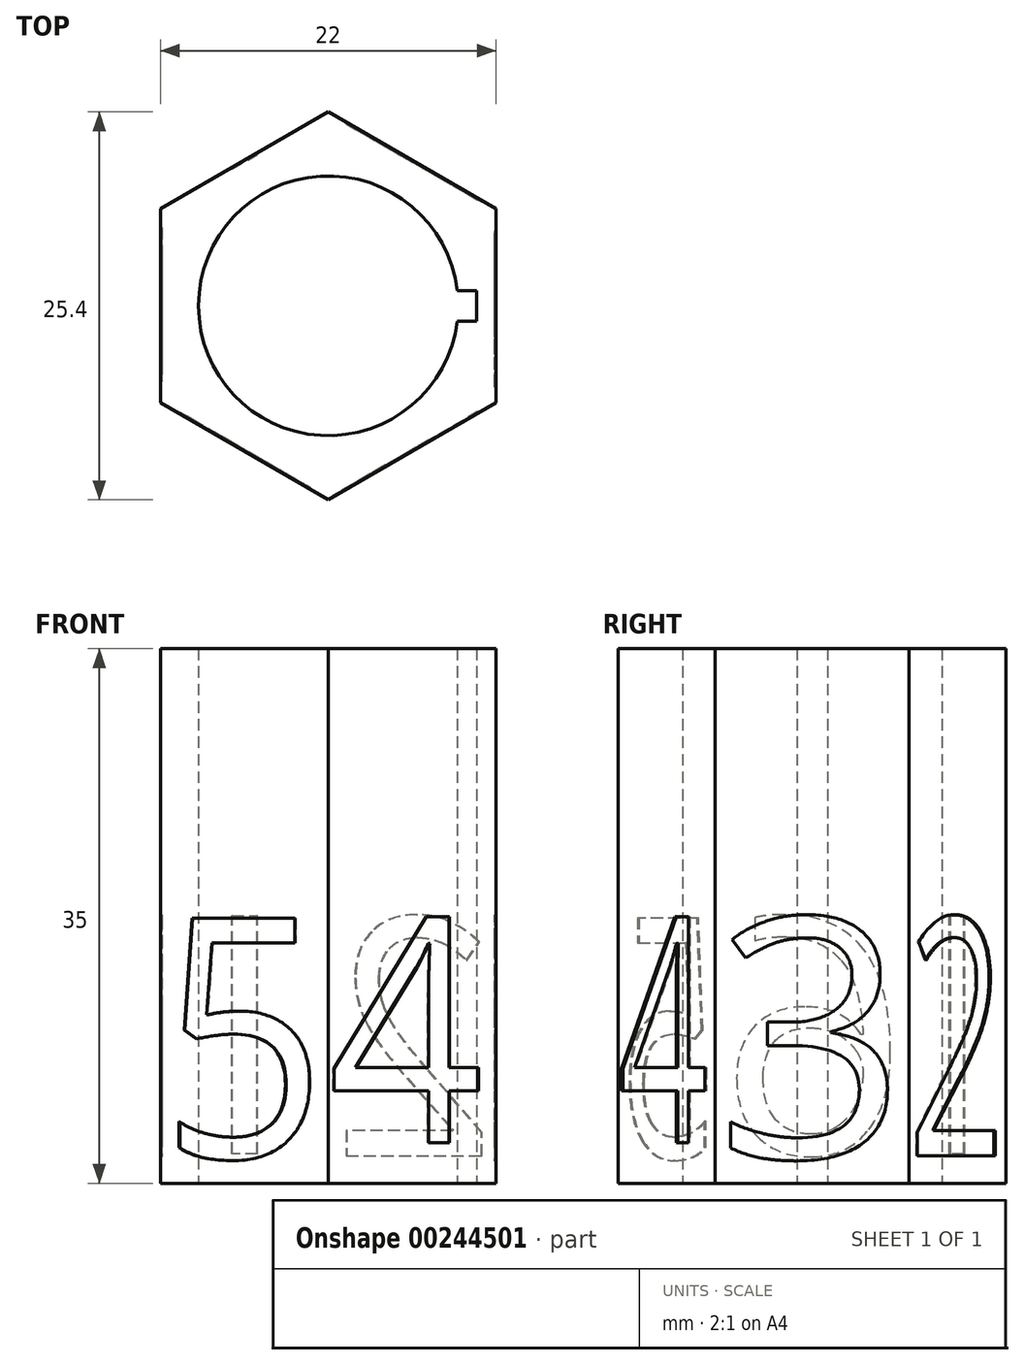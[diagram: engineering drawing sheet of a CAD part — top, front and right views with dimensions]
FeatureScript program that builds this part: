
annotation { "Feature Type Name" : "Feature", "Feature Type Description" : "" }
export const myFeature = defineFeature(function(context is Context, id is Id, definition is map)
    precondition{}
    {
        {
            var Q0;
            Q0=qCreatedBy(makeId("Top.planeOp"),FACE);
            var sketch = newSketch(context, id + "F0", { "sketchPlane" : qUnion([Q0])});
            skCircle(sketch, "E0", {"center": v(0, 0) * mm, "radius": 12.7 * mm});
            skCircle(sketch, "E1.cCircle", {"center": v(0, 0) * mm, "radius": 12.7 * mm, "construction": true});
            skLineSegment(sketch, "E1.0", {"start": v(0, 12.7) * mm, "end": v(11, 6.35) * mm});
            skLineSegment(sketch, "E1.1", {"start": v(11, 6.35) * mm, "end": v(11, -6.35) * mm});
            skLineSegment(sketch, "E1.2", {"start": v(11, -6.35) * mm, "end": v(0, -12.7) * mm});
            skLineSegment(sketch, "E1.3", {"start": v(0, -12.7) * mm, "end": v(-11, -6.35) * mm});
            skLineSegment(sketch, "E1.4", {"start": v(-11, -6.35) * mm, "end": v(-11, 6.35) * mm});
            skLineSegment(sketch, "E1.5", {"start": v(-11, 6.35) * mm, "end": v(0, 12.7) * mm});
            skSolve(sketch);
        }
        {
            var Q0;
            Q0=makeQuery(id+"F0.imprint","IMPRINT",FACE,{"disambiguationData":[TD([[makeQuery(id+"F0.imprint","IMPRINT",EDGE,{"derivedFrom":sQuery(id+"F0.wireOp",EDGE,"E1.0")}),-1.0]])]});
            extrude(context, id + "F1", {"entities" : qUnion([Q0]), "depth" : 35 * mm});
        }
        {
            var Q0;
            Q0=makeQuery(id+"F1.opExtrude","CAP_FACE",FACE,{"disambiguationData":[OSD([sQuery(id+"F0.wireOp",EDGE,"E1.0"),sQuery(id+"F0.wireOp",EDGE,"E1.1"),sQuery(id+"F0.wireOp",EDGE,"E1.2"),sQuery(id+"F0.wireOp",EDGE,"E1.3"),sQuery(id+"F0.wireOp",EDGE,"E1.4"),sQuery(id+"F0.wireOp",EDGE,"E1.5")])],"isStart":true});
            var sketch = newSketch(context, id + "F2", { "sketchPlane" : qUnion([Q0])});
            skArc(sketch, "E2", {"start": v(8.44, 1) * mm, "mid": v(-8.5, 0) * mm, "end": v(8.44, -1) * mm});
            skLineSegment(sketch, "E3", {"start": v(9.72, 1) * mm, "end": v(8.44, 1) * mm});
            skLineSegment(sketch, "E4", {"start": v(8.44, 1) * mm, "end": v(9.72, 1) * mm});
            skLineSegment(sketch, "E5", {"start": v(9.72, -1) * mm, "end": v(8.44, -1) * mm});
            skLineSegment(sketch, "E6", {"start": v(8.44, -1) * mm, "end": v(9.72, -1) * mm});
            skLineSegment(sketch, "E7", {"start": v(9.72, -1) * mm, "end": v(9.72, 1) * mm});
            skPoint(sketch, "E8.end.orphan", {"position": v(11, -1) * mm});
            skPoint(sketch, "E9.end.orphan", {"position": v(11, 1) * mm});
            skPoint(sketch, "E9.start.orphan", {"position": v(11, 0) * mm});
            skSolve(sketch);
        }
        {
            var Q0;
            Q0 = qSketchRegion(id + "F2", true);
            extrude(context, id + "F3", {"entities" : qUnion([Q0]), "operationType" : NewBodyOperationType.REMOVE, "oppositeDirection" : true, "depth" : 45 * mm});
        }
        {
            var Q0;
            Q0=makeQuery(id+"F1.opExtrude","SWEPT_FACE",FACE,{"disambiguationData":[OSD([sQuery(id+"F0.wireOp",EDGE,"E1.1")])]});
            var sketch = newSketch(context, id + "F4", { "sketchPlane" : qUnion([Q0])});
            skText(sketch, "E10", { "text": "3", "fontName": "OpenSans-Regular.ttf"});
            const initialGuessF4  = {"E10": [-0.00635, 0.00168, 1, 0, 0.01582]};
            skSetInitialGuess(sketch, initialGuessF4);
            skSolve(sketch);
        }
        {
            var Q0;
            Q0 = qSketchRegion(id + "F4", true);
            extrude(context, id + "F5", {"entities" : qUnion([Q0]), "operationType" : NewBodyOperationType.REMOVE, "oppositeDirection" : true, "depth" : .1 * mm});
        }
        {
            var Q0;
            Q0=makeQuery(id+"F1.opExtrude","SWEPT_FACE",FACE,{"disambiguationData":[OSD([sQuery(id+"F0.wireOp",EDGE,"E1.0")])]});
            var sketch = newSketch(context, id + "F6", { "sketchPlane" : qUnion([Q0])});
            skText(sketch, "E11", { "text": "2", "fontName": "OpenSans-Regular.ttf"});
            const initialGuessF6  = {"E11": [-0.00635, 0.00181, 1, 0, 0.01569]};
            skSetInitialGuess(sketch, initialGuessF6);
            skSolve(sketch);
        }
        {
            var Q0;
            Q0 = qSketchRegion(id + "F6", true);
            extrude(context, id + "F7", {"entities" : qUnion([Q0]), "operationType" : NewBodyOperationType.REMOVE, "oppositeDirection" : true, "depth" : .1 * mm});
        }
        {
            var Q0;
            Q0=makeQuery(id+"F1.opExtrude","SWEPT_FACE",FACE,{"disambiguationData":[OSD([sQuery(id+"F0.wireOp",EDGE,"E1.5")])]});
            var sketch = newSketch(context, id + "F8", { "sketchPlane" : qUnion([Q0])});
            skLineSegment(sketch, "E12", {"start": v(0, 0) * mm, "end": v(6.35, 0) * mm});
            skLineSegment(sketch, "E13", {"start": v(6.35, 0) * mm, "end": v(6.35, 17.5) * mm});
            skLineSegment(sketch, "E14", {"start": v(6.35, 17.5) * mm, "end": v(-6.35, 17.5) * mm});
            skLineSegment(sketch, "E15.top", {"start": v(0.95, 33.38) * mm, "end": v(-0.95, 33.38) * mm});
            skLineSegment(sketch, "E15.left", {"start": v(0.95, 1.93) * mm, "end": v(0.95, 33.38) * mm});
            skLineSegment(sketch, "E15.right", {"start": v(-0.95, 1.93) * mm, "end": v(-0.95, 33.38) * mm});
            skPoint(sketch, "E15.middle", {"position": v(0, 17.5) * mm});
            skLineSegment(sketch, "E16", {"start": v(-0.95, 1.93) * mm, "end": v(0.95, 1.93) * mm});
            skPoint(sketch, "E15.bottom.start.orphan", {"position": v(0.95, 1.62) * mm});
            skPoint(sketch, "E17.orphan", {"position": v(-0.95, 1.62) * mm});
            skSolve(sketch);
        }
        {
            var Q0;
            {var subQ5=sQuery(id+"F8.wireOp",EDGE,"E16");Q0=makeQuery(id+"F8.imprint","IMPRINT",FACE,{"disambiguationData":[TD([[makeQuery(id+"F8.imprint","IMPRINT",EDGE,{"derivedFrom":subQ5}),1.0]])]});}
            extrude(context, id + "F9", {"entities" : qUnion([Q0]), "operationType" : NewBodyOperationType.REMOVE, "oppositeDirection" : true, "depth" : .1 * mm});
        }
        {
            var Q0;
            Q0=makeQuery(id+"F1.opExtrude","SWEPT_FACE",FACE,{"disambiguationData":[OSD([sQuery(id+"F0.wireOp",EDGE,"E1.4")])]});
            var sketch = newSketch(context, id + "F10", { "sketchPlane" : qUnion([Q0])});
            skText(sketch, "E18", { "text": "6\n", "fontName": "OpenSans-Regular.ttf"});
            const initialGuessF10  = {"E18": [-0.00635, 0.00194, 1, 0, 0.01556]};
            skSetInitialGuess(sketch, initialGuessF10);
            skSolve(sketch);
        }
        {
            var Q0;
            Q0 = qSketchRegion(id + "F10", true);
            extrude(context, id + "F11", {"entities" : qUnion([Q0]), "operationType" : NewBodyOperationType.REMOVE, "oppositeDirection" : true, "depth" : .1 * mm});
        }
        {
            var Q0;
            Q0=makeQuery(id+"F1.opExtrude","SWEPT_FACE",FACE,{"disambiguationData":[OSD([sQuery(id+"F0.wireOp",EDGE,"E1.3")])]});
            var sketch = newSketch(context, id + "F12", { "sketchPlane" : qUnion([Q0])});
            skText(sketch, "E19", { "text": "5", "fontName": "OpenSans-Regular.ttf"});
            const initialGuessF12  = {"E19": [-0.00635, 0.0017, 1, 0, 0.0158]};
            skSetInitialGuess(sketch, initialGuessF12);
            skSolve(sketch);
        }
        {
            var Q0;
            Q0 = qSketchRegion(id + "F12", true);
            extrude(context, id + "F13", {"entities" : qUnion([Q0]), "operationType" : NewBodyOperationType.REMOVE, "oppositeDirection" : true, "depth" : .1 * mm});
        }
        {
            var Q0;
            Q0=makeQuery(id+"F1.opExtrude","SWEPT_FACE",FACE,{"disambiguationData":[OSD([sQuery(id+"F0.wireOp",EDGE,"E1.2")])]});
            var sketch = newSketch(context, id + "F14", { "sketchPlane" : qUnion([Q0])});
            skText(sketch, "E20", { "text": "4", "fontName": "OpenSans-Regular.ttf"});
            const initialGuessF14  = {"E20": [-0.00635, 0.00267, 1, 0, 0.01483]};
            skSetInitialGuess(sketch, initialGuessF14);
            skSolve(sketch);
        }
        {
            var Q0;
            Q0 = qSketchRegion(id + "F14", true);
            extrude(context, id + "F15", {"entities" : qUnion([Q0]), "operationType" : NewBodyOperationType.REMOVE, "oppositeDirection" : true, "depth" : .1 * mm});
        }
    });
